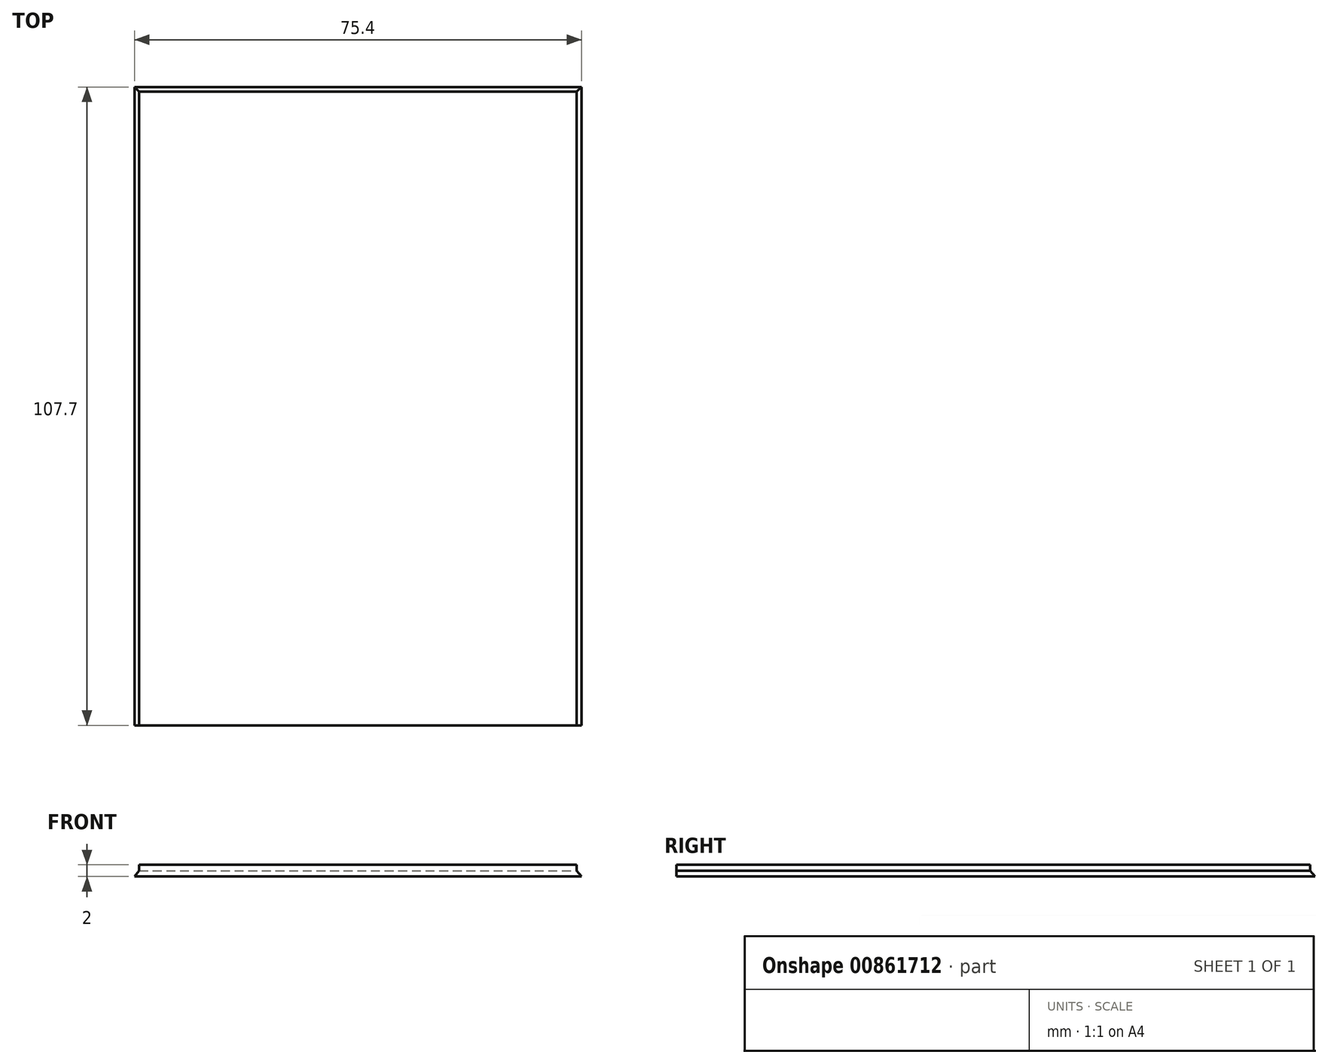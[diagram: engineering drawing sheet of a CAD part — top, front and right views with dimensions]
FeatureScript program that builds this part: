
annotation { "Feature Type Name" : "Feature", "Feature Type Description" : "" }
export const myFeature = defineFeature(function(context is Context, id is Id, definition is map)
    precondition{}
    {
        {
            var Q0;
            Q0=qCreatedBy(makeId("Front.planeOp"),FACE);
            var sketch = newSketch(context, id + "F0", { "sketchPlane" : qUnion([Q0])});
            skLineSegment(sketch, "E0", {"start": v(0.8, 1) * mm, "end": v(0.8, 2) * mm});
            skLineSegment(sketch, "E1", {"start": v(0.8, 2) * mm, "end": v(74.6, 2) * mm});
            skLineSegment(sketch, "E2", {"start": v(74.6, 2) * mm, "end": v(74.6, 1) * mm});
            skLineSegment(sketch, "E3", {"start": v(75.4, 0) * mm, "end": v(0, 0) * mm});
            skLineSegment(sketch, "E4", {"start": v(0, 0) * mm, "end": v(0.8, 1) * mm});
            skLineSegment(sketch, "E5", {"start": v(74.6, 1) * mm, "end": v(75.4, 0) * mm});
            skSolve(sketch);
        }
        {
            var Q0;
            Q0=qSketchRegion(id+"F0",true);
            extrude(context, id + "F1", {"entities" : qUnion([Q0]), "oppositeDirection" : true, "depth" : 109 * mm, "offsetDistance" : 25 * mm});
        }
        {
            var Q0;
            Q0=makeQuery(id+"F1.opExtrude","SWEPT_FACE",FACE,{"disambiguationData":[OSD([sQuery(id+"F0.wireOp",EDGE,"E2")])]});
            var sketch = newSketch(context, id + "F2", { "sketchPlane" : qUnion([Q0])});
            skLineSegment(sketch, "E6", {"start": v(109, 2) * mm, "end": v(106.9, 2) * mm});
            skLineSegment(sketch, "E7", {"start": v(106.9, 2) * mm, "end": v(106.9, 1) * mm});
            skLineSegment(sketch, "E8", {"start": v(106.9, 1) * mm, "end": v(107.7, 0) * mm});
            skLineSegment(sketch, "E9", {"start": v(107.7, 0) * mm, "end": v(109, 0) * mm});
            skLineSegment(sketch, "E10", {"start": v(109, 0) * mm, "end": v(109, 2) * mm});
            skSolve(sketch);
        }
        {
            var Q0;
            Q0=qSketchRegion(id+"F2",true);
            extrude(context, id + "F3", {"entities" : qUnion([Q0]), "operationType" : NewBodyOperationType.REMOVE, "endBound" : BoundingType.SYMMETRIC, "oppositeDirection" : true, "depth" : 159.4 * mm, "offsetDistance" : 25 * mm});
        }
    });
